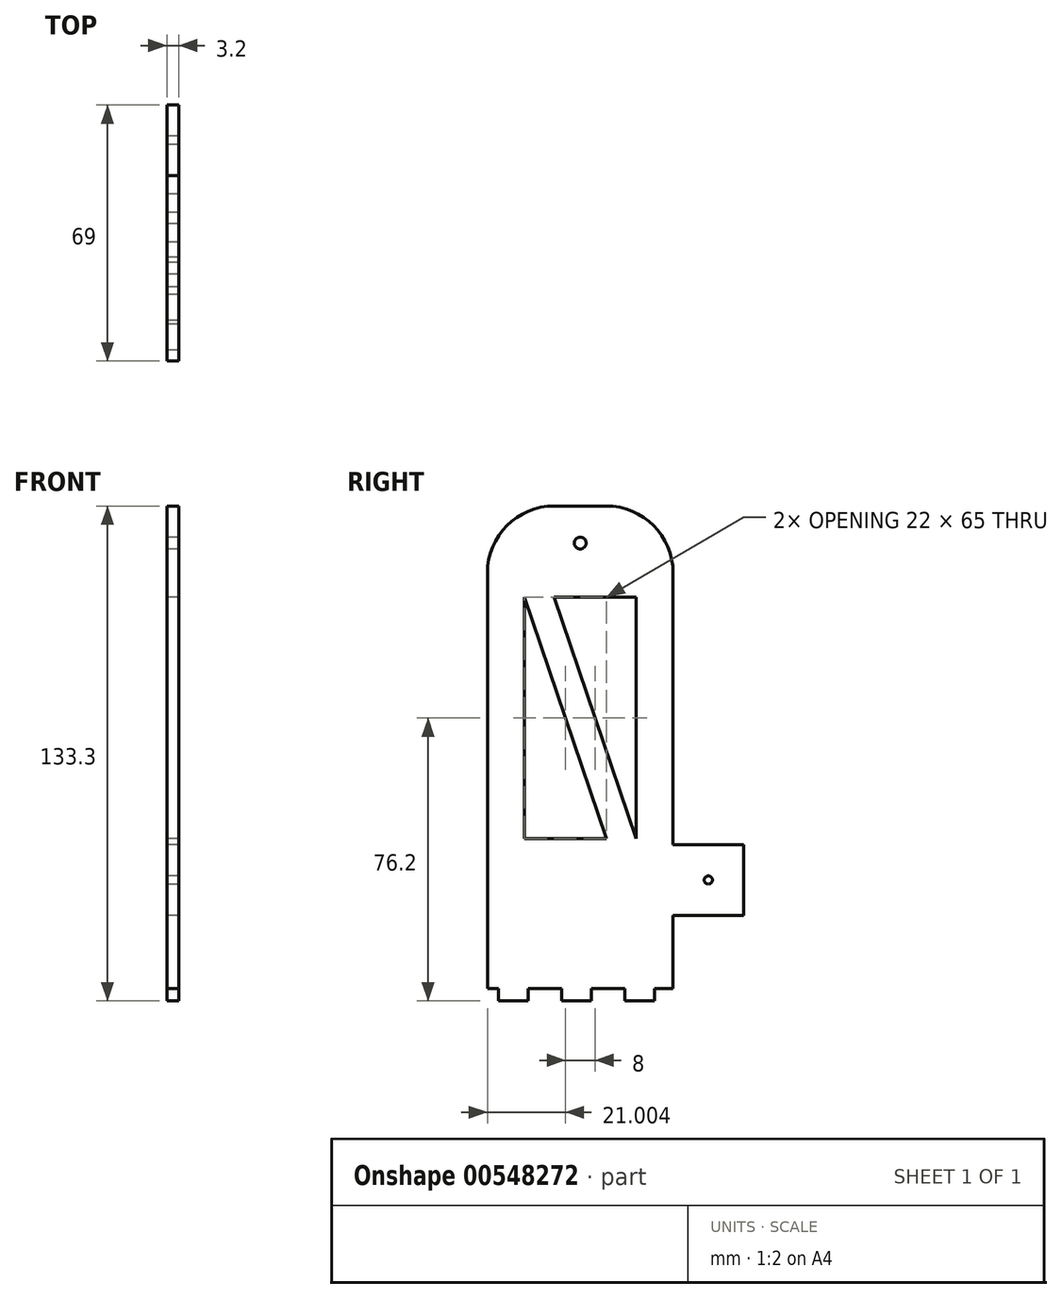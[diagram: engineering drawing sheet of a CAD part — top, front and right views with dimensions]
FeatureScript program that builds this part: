
annotation { "Feature Type Name" : "Feature", "Feature Type Description" : "" }
export const myFeature = defineFeature(function(context is Context, id is Id, definition is map)
    precondition{}
    {
        {
            var Q0;
            Q0=qCreatedBy(makeId("Right.planeOp"),FACE);
            var sketch = newSketch(context, id + "F0", { "sketchPlane" : qUnion([Q0])});
            skLineSegment(sketch, "E0", {"start": v(-34.76, 112) * mm, "end": v(-34.76, 0) * mm});
            skLineSegment(sketch, "E1", {"start": v(-34.76, 0) * mm, "end": v(15.24, 0) * mm});
            skLineSegment(sketch, "E2", {"start": v(15.24, 0) * mm, "end": v(15.24, 112) * mm});
            skLineSegment(sketch, "E3", {"start": v(-2.76, 130) * mm, "end": v(-16.76, 130) * mm});
            skPoint(sketch, "E4.visualSharp", {"position": v(-34.76, 130) * mm});
            skArc(sketch, "E4.filletArc", {"start": v(-16.76, 130) * mm, "mid": v(-29.48, 124.73) * mm, "end": v(-34.76, 112) * mm});
            skPoint(sketch, "E5.visualSharp", {"position": v(15.24, 130) * mm});
            skArc(sketch, "E5.filletArc", {"start": v(15.24, 112) * mm, "mid": v(9.97, 124.73) * mm, "end": v(-2.76, 130) * mm});
            skCircle(sketch, "E6", {"center": v(-9.76, 120) * mm, "radius": 1.6 * mm});
            skLineSegment(sketch, "E7", {"start": v(-31.76, -3.3) * mm, "end": v(-23.76, -3.3) * mm});
            skLineSegment(sketch, "E8", {"start": v(-23.76, -3.3) * mm, "end": v(-23.76, 0) * mm});
            skLineSegment(sketch, "E9", {"start": v(-14.76, 0) * mm, "end": v(-14.76, -3.3) * mm});
            skLineSegment(sketch, "E10", {"start": v(-14.76, -3.3) * mm, "end": v(-6.76, -3.3) * mm});
            skLineSegment(sketch, "E11", {"start": v(-6.76, -3.3) * mm, "end": v(-6.76, 0) * mm});
            skLineSegment(sketch, "E12", {"start": v(2.24, 0) * mm, "end": v(2.24, -3.3) * mm});
            skLineSegment(sketch, "E13", {"start": v(2.24, -3.3) * mm, "end": v(10.24, -3.3) * mm});
            skLineSegment(sketch, "E14", {"start": v(10.24, -3.3) * mm, "end": v(10.24, 0) * mm});
            skLineSegment(sketch, "E15", {"start": v(-31.76, -3.3) * mm, "end": v(-31.76, 0) * mm});
            skLineSegment(sketch, "E16.bottom", {"start": v(-24.76, 105.4) * mm, "end": v(5.24, 105.4) * mm});
            skLineSegment(sketch, "E16.top", {"start": v(-24.76, 40.4) * mm, "end": v(5.24, 40.4) * mm});
            skLineSegment(sketch, "E16.left", {"start": v(-24.76, 105.4) * mm, "end": v(-24.76, 40.4) * mm});
            skLineSegment(sketch, "E16.right", {"start": v(5.24, 105.4) * mm, "end": v(5.24, 40.4) * mm});
            skLineSegment(sketch, "E17", {"start": v(-24.76, 105.4) * mm, "end": v(-2.76, 40.4) * mm});
            skLineSegment(sketch, "E18", {"start": v(-16.76, 105.4) * mm, "end": v(5.24, 40.4) * mm});
            skLineSegment(sketch, "E19.bottom", {"start": v(15.24, 38.75) * mm, "end": v(34.24, 38.75) * mm});
            skLineSegment(sketch, "E19.top", {"start": v(15.24, 19.75) * mm, "end": v(34.24, 19.75) * mm});
            skLineSegment(sketch, "E19.left", {"start": v(15.24, 38.75) * mm, "end": v(15.24, 19.75) * mm});
            skLineSegment(sketch, "E19.right", {"start": v(34.24, 38.75) * mm, "end": v(34.24, 19.75) * mm});
            skCircle(sketch, "E20", {"center": v(24.74, 29.25) * mm, "radius": 1.1 * mm});
            skSolve(sketch);
        }
        {
            var Q0;
            Q0=qSketchRegion(id+"F0",true);
            var Q1;
            {var subQ0=sQuery(id+"F0.wireOp",EDGE,"UKrZW6tz-tfzN-KJjJ-yuHU-Zlwch0H15JHo");Q1=makeQuery(id+"F0.imprint","IMPRINT",FACE,{"disambiguationData":[TD([[makeQuery(id+"F0.imprint","IMPRINT",EDGE,{"derivedFrom":subQ0}),1.0]])]});}
            var Q2;
            {var subQ0=sQuery(id+"F0.wireOp",EDGE,"E17");Q2=makeQuery(id+"F0.imprint","IMPRINT",FACE,{"disambiguationData":[TD([[makeQuery(id+"F0.imprint","IMPRINT",EDGE,{"derivedFrom":subQ0}),1.0]])]});}
            extrude(context, id + "F1", {"entities" : qUnion([Q0, Q1, Q2]), "depth" : 3.2 * mm, "offsetDistance" : 25 * mm});
        }
    });
